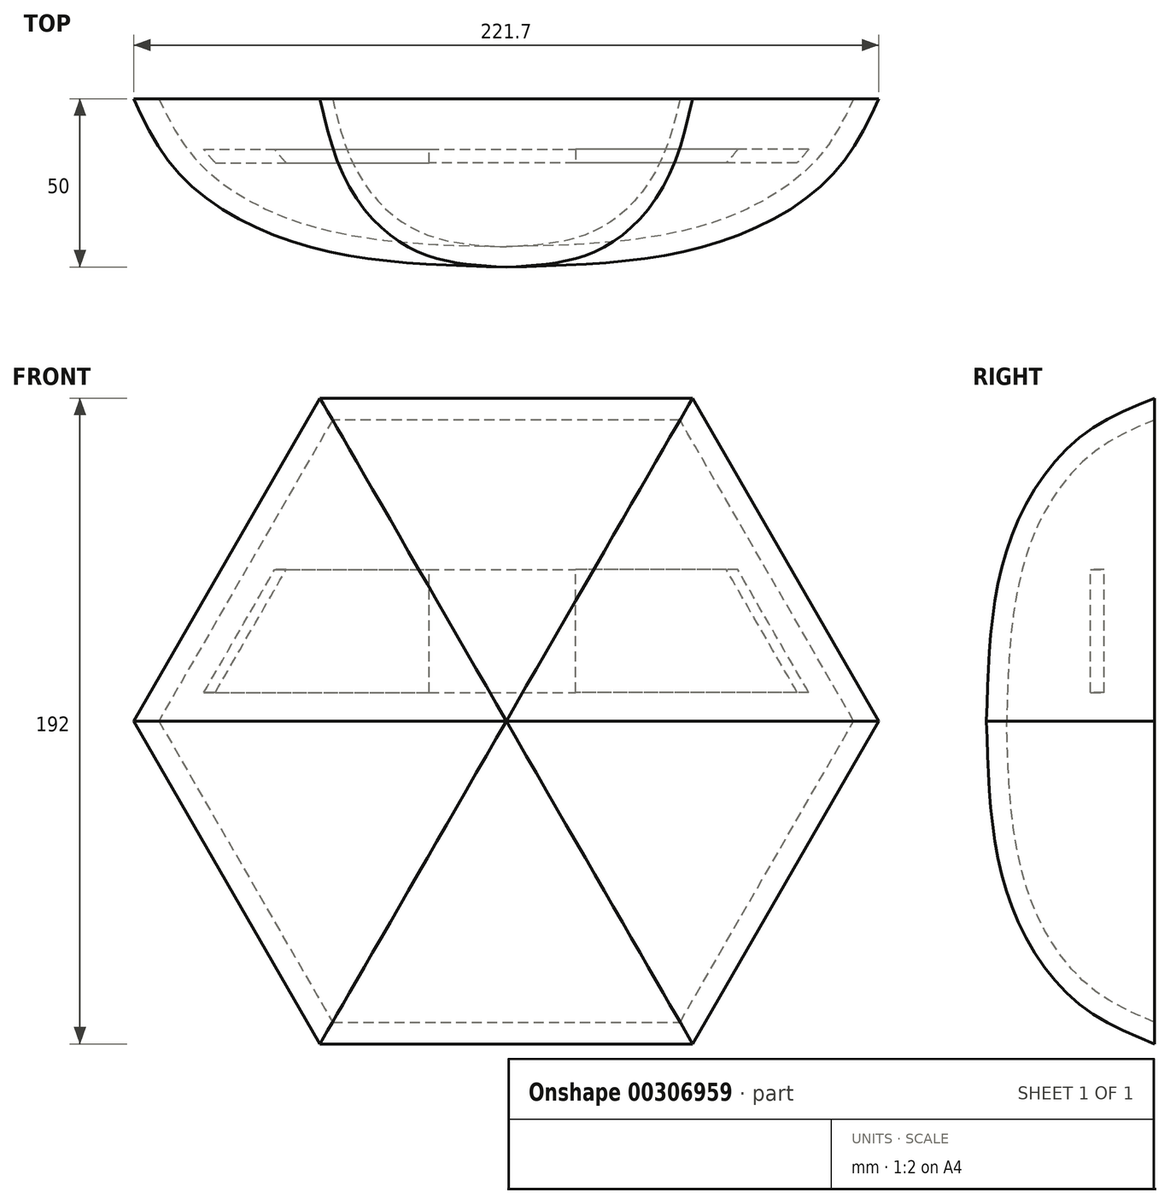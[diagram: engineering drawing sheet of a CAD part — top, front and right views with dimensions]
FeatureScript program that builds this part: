
annotation { "Feature Type Name" : "Feature", "Feature Type Description" : "" }
export const myFeature = defineFeature(function(context is Context, id is Id, definition is map)
    precondition{}
    {
        {
            var Q0;
            Q0=qCreatedBy(makeId("Front.planeOp"),FACE);
            var sketch = newSketch(context, id + "F0", { "sketchPlane" : qUnion([Q0])});
            skCircle(sketch, "E0.cCircle", {"center": v(0, 0) * mm, "radius": 96 * mm, "construction": true});
            skLineSegment(sketch, "E0.0", {"start": v(-55.43, 96) * mm, "end": v(55.43, 96) * mm});
            skLineSegment(sketch, "E0.1", {"start": v(55.43, 96) * mm, "end": v(110.85, 0) * mm});
            skLineSegment(sketch, "E0.2", {"start": v(110.85, 0) * mm, "end": v(55.43, -96) * mm});
            skLineSegment(sketch, "E0.3", {"start": v(55.43, -96) * mm, "end": v(-55.43, -96) * mm});
            skLineSegment(sketch, "E0.4", {"start": v(-55.43, -96) * mm, "end": v(-110.85, 0) * mm});
            skLineSegment(sketch, "E0.5", {"start": v(-110.85, 0) * mm, "end": v(-55.43, 96) * mm});
            skPoint(sketch, "E0.0.midPoint", {"position": v(0, 96) * mm});
            skSolve(sketch);
        }
        {
            var Q0;
            Q0=qCreatedBy(makeId("Front.planeOp"),FACE);
            cPlane(context, id + "F1", {"entities" : qUnion([Q0]), "cplaneType" : CPlaneType.OFFSET, "offset" : 20 * mm, "width" : 150 * mm, "height" : 150 * mm});
        }
        {
            var Q0;
            Q0=qCreatedBy(id+"F1.planeOp",FACE);
            var sketch = newSketch(context, id + "F2", { "sketchPlane" : qUnion([Q0])});
            skCircle(sketch, "E1.cCircle", {"center": v(0, 0) * mm, "radius": 86 * mm, "construction": true});
            skLineSegment(sketch, "E1.0", {"start": v(-49.65, 86) * mm, "end": v(49.65, 86) * mm});
            skLineSegment(sketch, "E1.1", {"start": v(49.65, 86) * mm, "end": v(99.3, 0) * mm});
            skLineSegment(sketch, "E1.2", {"start": v(99.3, 0) * mm, "end": v(49.65, -86) * mm});
            skLineSegment(sketch, "E1.3", {"start": v(49.65, -86) * mm, "end": v(-49.65, -86) * mm});
            skLineSegment(sketch, "E1.4", {"start": v(-49.65, -86) * mm, "end": v(-99.3, 0) * mm});
            skLineSegment(sketch, "E1.5", {"start": v(-99.3, 0) * mm, "end": v(-49.65, 86) * mm});
            skPoint(sketch, "E1.0.midPoint", {"position": v(0, 86) * mm});
            skSolve(sketch);
        }
        {
            var Q0;
            Q0=qCreatedBy(id+"F1.planeOp",FACE);
            cPlane(context, id + "F3", {"entities" : qUnion([Q0]), "cplaneType" : CPlaneType.OFFSET, "offset" : 20 * mm, "width" : 150 * mm, "height" : 150 * mm});
        }
        {
            var Q0;
            Q0=qCreatedBy(id+"F3.planeOp",FACE);
            var sketch = newSketch(context, id + "F4", { "sketchPlane" : qUnion([Q0])});
            skCircle(sketch, "E2.cCircle", {"center": v(0, 0) * mm, "radius": 61 * mm, "construction": true});
            skLineSegment(sketch, "E2.0", {"start": v(-35.22, 61) * mm, "end": v(35.22, 61) * mm});
            skLineSegment(sketch, "E2.1", {"start": v(35.22, 61) * mm, "end": v(70.44, 0) * mm});
            skLineSegment(sketch, "E2.2", {"start": v(70.44, 0) * mm, "end": v(35.22, -61) * mm});
            skLineSegment(sketch, "E2.3", {"start": v(35.22, -61) * mm, "end": v(-35.22, -61) * mm});
            skLineSegment(sketch, "E2.4", {"start": v(-35.22, -61) * mm, "end": v(-70.44, 0) * mm});
            skLineSegment(sketch, "E2.5", {"start": v(-70.44, 0) * mm, "end": v(-35.22, 61) * mm});
            skPoint(sketch, "E2.0.midPoint", {"position": v(0, 61) * mm});
            skSolve(sketch);
        }
        {
            var Q0;
            Q0=qCreatedBy(id+"F3.planeOp",FACE);
            cPlane(context, id + "F5", {"entities" : qUnion([Q0]), "cplaneType" : CPlaneType.OFFSET, "offset" : 10 * mm, "width" : 150 * mm, "height" : 150 * mm});
        }
        {
            var Q0;
            Q0=qCreatedBy(id+"F5.planeOp",FACE);
            var sketch = newSketch(context, id + "F6", { "sketchPlane" : qUnion([Q0])});
            skPoint(sketch, "E3", {"position": v(0, 0) * mm});
            skSolve(sketch);
        }
        {
            var Q0;
            Q0=makeQuery(id+"F0.imprint","IMPRINT",FACE,{"disambiguationData":[TD([[makeQuery(id+"F0.imprint","IMPRINT",EDGE,{"derivedFrom":sQuery(id+"F0.wireOp",EDGE,"E0.0")}),-1.0]])]});
            var Q1;
            Q1=makeQuery(id+"F2.imprint","IMPRINT",FACE,{"disambiguationData":[TD([[makeQuery(id+"F2.imprint","IMPRINT",EDGE,{"derivedFrom":sQuery(id+"F2.wireOp",EDGE,"E1.0")}),-1.0]])]});
            var Q2;
            Q2=makeQuery(id+"F4.imprint","IMPRINT",FACE,{"disambiguationData":[TD([[makeQuery(id+"F4.imprint","IMPRINT",EDGE,{"derivedFrom":sQuery(id+"F4.wireOp",EDGE,"E2.0")}),-1.0]])]});
            var Q3;
            Q3=sQuery(id+"F6.wireOp",VERTEX,"E3");
            loft(context, id + "F7", {"sheetProfilesArray" : [{ "sheetProfileEntities" : qUnion([Q0]) }, { "sheetProfileEntities" : qUnion([Q1]) }, { "sheetProfileEntities" : qUnion([Q2]) }, { "sheetProfileEntities" : qUnion([Q3]) }]});
        }
        {
            var Q0;
            Q0=makeQuery(id+"F7.opLoft","CAP_FACE",FACE,{"disambiguationData":[OSD([makeQuery(id+"F0.imprint","IMPRINT",FACE,{"disambiguationData":[TD([[makeQuery(id+"F0.imprint","IMPRINT",EDGE,{"derivedFrom":sQuery(id+"F0.wireOp",EDGE,"E0.0")}),-1.0]])]})])],"isStart":true});
            shell(context, id + "F8", {"entities" : qUnion([Q0]), "thickness" : 6 * mm});
        }
        {
            var Q0;
            Q0=qCreatedBy(makeId("Top.planeOp"),FACE);
            cPlane(context, id + "F9", {"entities" : qUnion([Q0]), "cplaneType" : CPlaneType.OFFSET, "offset" : 45 * mm, "width" : 150 * mm, "height" : 150 * mm});
        }
        {
            var Q0;
            Q0=qCreatedBy(id+"F9.planeOp",FACE);
            var sketch = newSketch(context, id + "F10", { "sketchPlane" : qUnion([Q0])});
            skLineSegment(sketch, "E4", {"start": v(-22.97, -15) * mm, "end": v(20.65, -15) * mm});
            skLineSegment(sketch, "E5", {"start": v(20.65, -15) * mm, "end": v(20.65, -19) * mm});
            skLineSegment(sketch, "E6", {"start": v(20.65, -19) * mm, "end": v(-22.97, -19) * mm});
            skLineSegment(sketch, "E7", {"start": v(-22.97, -19) * mm, "end": v(-22.97, -15) * mm});
            skSolve(sketch);
        }
        {
            var Q0;
            Q0 = qSketchRegion(id + "F10", true);
            extrude(context, id + "F11", {"entities" : qUnion([Q0]), "oppositeDirection" : true, "depth" : 36.5 * mm});
        }
        {
            var Q0;
            Q0=makeQuery(id+"F11.opExtrude","SWEPT_FACE",FACE,{"disambiguationData":[OSD([sQuery(id+"F10.wireOp",EDGE,"E5")])]});
            extrude(context, id + "F12", {"entities" : qUnion([Q0]), "endBound" : BoundingType.UP_TO_NEXT, "depth" : 25 * mm});
        }
        {
            var Q0;
            Q0=makeQuery(id+"F11.opExtrude","SWEPT_FACE",FACE,{"disambiguationData":[OSD([sQuery(id+"F10.wireOp",EDGE,"E7")])]});
            extrude(context, id + "F13", {"entities" : qUnion([Q0]), "endBound" : BoundingType.UP_TO_NEXT, "depth" : 25 * mm});
        }
    });
